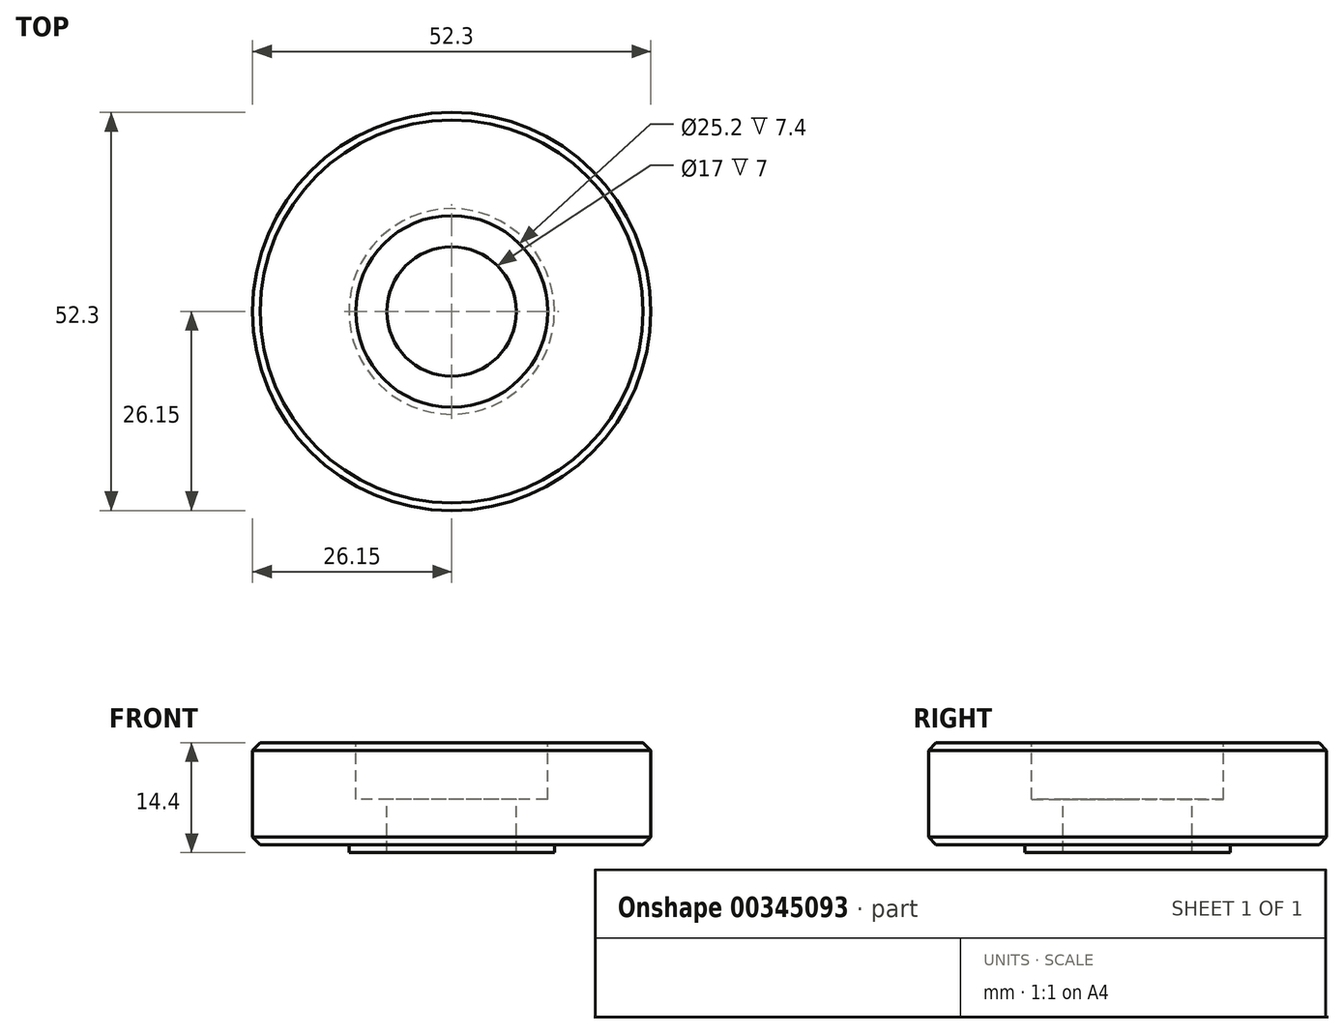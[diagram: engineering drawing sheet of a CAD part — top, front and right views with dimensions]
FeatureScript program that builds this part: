
annotation { "Feature Type Name" : "Feature", "Feature Type Description" : "" }
export const myFeature = defineFeature(function(context is Context, id is Id, definition is map)
    precondition{}
    {
        {
            var Q0;
            Q0=qCreatedBy(makeId("Top.planeOp"),FACE);
            var sketch = newSketch(context, id + "F0", { "sketchPlane" : qUnion([Q0])});
            skCircle(sketch, "E0", {"center": v(0, 0) * mm, "radius": 26.15 * mm});
            skSolve(sketch);
        }
        {
            var Q0;
            Q0 = qSketchRegion(id + "F0", true);
            extrude(context, id + "F1", {"entities" : qUnion([Q0]), "depth" : 13.4 * mm});
        }
        {
            var Q0;
            Q0=makeQuery(id+"F1.opExtrude","CAP_FACE",FACE,{"disambiguationData":[OSD([sQuery(id+"F0.wireOp",EDGE,"E0")])],"isStart":false});
            var sketch = newSketch(context, id + "F2", { "sketchPlane" : qUnion([Q0])});
            skCircle(sketch, "E1", {"center": v(0, 0) * mm, "radius": 12.6 * mm});
            skSolve(sketch);
        }
        {
            var Q0;
            Q0 = qSketchRegion(id + "F2", true);
            extrude(context, id + "F3", {"entities" : qUnion([Q0]), "operationType" : NewBodyOperationType.REMOVE, "oppositeDirection" : true, "depth" : 7.4 * mm});
        }
        {
            var Q0;
            Q0=makeQuery(id+"F3.boolean.opBoolean","COPY",FACE,{"derivedFrom":makeQuery(id+"F3.opExtrude","CAP_FACE",FACE,{"disambiguationData":[OSD([sQuery(id+"F2.wireOp",EDGE,"E1")])],"isStart":false})});
            var sketch = newSketch(context, id + "F4", { "sketchPlane" : qUnion([Q0])});
            skCircle(sketch, "E2", {"center": v(0, 0) * mm, "radius": 8.5 * mm});
            skSolve(sketch);
        }
        {
            var Q0;
            Q0=makeQuery(id+"F4.imprint","IMPRINT",FACE,{"disambiguationData":[TD([[makeQuery(id+"F4.imprint","IMPRINT",EDGE,{"derivedFrom":sQuery(id+"F4.wireOp",EDGE,"E2")}),1.0]])]});
            extrude(context, id + "F5", {"entities" : qUnion([Q0]), "operationType" : NewBodyOperationType.REMOVE, "endBound" : BoundingType.UP_TO_NEXT, "oppositeDirection" : true, "depth" : 25 * mm});
        }
        {
            var Q0;
            Q0=makeQuery(id+"F1.opExtrude","CAP_FACE",FACE,{"disambiguationData":[OSD([sQuery(id+"F0.wireOp",EDGE,"E0")])],"isStart":true});
            var sketch = newSketch(context, id + "F6", { "sketchPlane" : qUnion([Q0])});
            skCircle(sketch, "E3", {"center": v(0, 0) * mm, "radius": 13.5 * mm});
            skCircle(sketch, "E4", {"center": v(0, 0) * mm, "radius": 8.5 * mm});
            skSolve(sketch);
        }
        {
            var Q0;
            Q0 = qSketchRegion(id + "F6", true);
            extrude(context, id + "F7", {"entities" : qUnion([Q0]), "operationType" : NewBodyOperationType.ADD, "depth" : 1 * mm});
        }
        {
            var Q0;
            Q0=makeQuery(id+"F1.opExtrude","CAP_EDGE",EDGE,{"disambiguationData":[OSD([sQuery(id+"F0.wireOp",EDGE,"E0")])],"isStart":false});
            var Q1;
            Q1=makeQuery(id+"F1.opExtrude","CAP_EDGE",EDGE,{"disambiguationData":[OSD([sQuery(id+"F0.wireOp",EDGE,"E0")])],"isStart":true});
            chamfer(context, id + "F8", {"entities" : qUnion([Q0, Q1]), "width" : 1 * mm, "tangentPropagation" : true});
        }
    });
